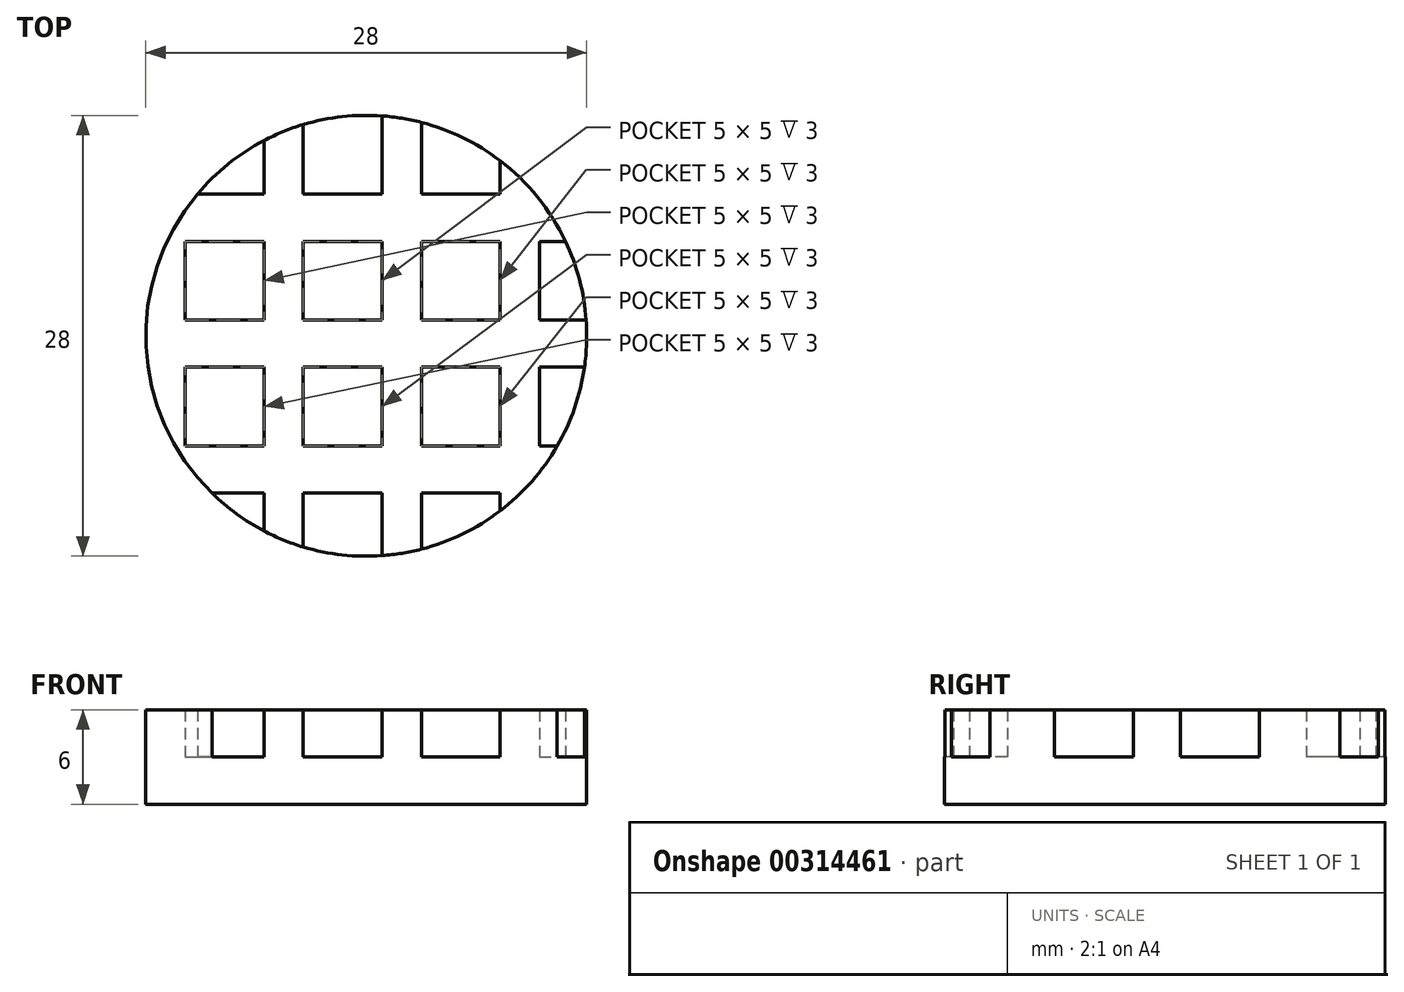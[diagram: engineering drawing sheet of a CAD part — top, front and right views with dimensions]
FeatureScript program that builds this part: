
annotation { "Feature Type Name" : "Feature", "Feature Type Description" : "" }
export const myFeature = defineFeature(function(context is Context, id is Id, definition is map)
    precondition{}
    {
        {
            var Q0;
            Q0=qCreatedBy(makeId("Top.planeOp"),FACE);
            var sketch = newSketch(context, id + "F0", { "sketchPlane" : qUnion([Q0])});
            skCircle(sketch, "E0", {"center": v(0, 0) * mm, "radius": 14 * mm});
            skSolve(sketch);
        }
        {
            var Q0;
            Q0=makeQuery(id+"F0.imprint","IMPRINT",FACE,{"disambiguationData":[TD([[makeQuery(id+"F0.imprint","IMPRINT",EDGE,{"derivedFrom":sQuery(id+"F0.wireOp",EDGE,"E0")}),1.0]])]});
            extrude(context, id + "F1", {"entities" : qUnion([Q0]), "depth" : 3 * mm});
        }
        {
            var Q0;
            Q0=makeQuery(id+"F1.opExtrude","CAP_FACE",FACE,{"disambiguationData":[OSD([sQuery(id+"F0.wireOp",EDGE,"E0")])],"isStart":false});
            var sketch = newSketch(context, id + "F2", { "sketchPlane" : qUnion([Q0])});
            skLineSegment(sketch, "E1.bottom", {"start": v(-11.5, 14) * mm, "end": v(-6.5, 14) * mm});
            skLineSegment(sketch, "E1.top", {"start": v(-11.5, 9) * mm, "end": v(-6.5, 9) * mm});
            skLineSegment(sketch, "E1.left", {"start": v(-11.5, 14) * mm, "end": v(-11.5, 9) * mm});
            skLineSegment(sketch, "E1.right", {"start": v(-6.5, 14) * mm, "end": v(-6.5, 9) * mm});
            skLineSegment(sketch, "E2.1.0.0", {"start": v(-4, 9) * mm, "end": v(1, 9) * mm});
            skLineSegment(sketch, "E2.1.0.1", {"start": v(-4, 14) * mm, "end": v(-4, 9) * mm});
            skLineSegment(sketch, "E2.1.0.2", {"start": v(1, 14) * mm, "end": v(1, 9) * mm});
            skLineSegment(sketch, "E2.1.0.3", {"start": v(-4, 14) * mm, "end": v(1, 14) * mm});
            skLineSegment(sketch, "E2.2.0.0", {"start": v(3.5, 9) * mm, "end": v(8.5, 9) * mm});
            skLineSegment(sketch, "E2.2.0.1", {"start": v(3.5, 14) * mm, "end": v(3.5, 9) * mm});
            skLineSegment(sketch, "E2.2.0.2", {"start": v(8.5, 14) * mm, "end": v(8.5, 9) * mm});
            skLineSegment(sketch, "E2.2.0.3", {"start": v(3.5, 14) * mm, "end": v(8.5, 14) * mm});
            skLineSegment(sketch, "E2.direction1", {"start": v(-11.5, 9) * mm, "end": v(-4, 9) * mm, "construction": true});
            skLineSegment(sketch, "E3.0.3.0", {"start": v(11, 9) * mm, "end": v(16, 9) * mm});
            skLineSegment(sketch, "E3.3.3.0", {"start": v(11, 14) * mm, "end": v(11, 9) * mm});
            skLineSegment(sketch, "E3.6.3.0", {"start": v(16, 14) * mm, "end": v(16, 9) * mm});
            skLineSegment(sketch, "E3.9.3.0", {"start": v(11, 14) * mm, "end": v(16, 14) * mm});
            skLineSegment(sketch, "E4.0.4.0", {"start": v(18.5, 9) * mm, "end": v(23.5, 9) * mm});
            skLineSegment(sketch, "E4.3.4.0", {"start": v(18.5, 14) * mm, "end": v(18.5, 9) * mm});
            skLineSegment(sketch, "E4.6.4.0", {"start": v(23.5, 14) * mm, "end": v(23.5, 9) * mm});
            skLineSegment(sketch, "E4.9.4.0", {"start": v(18.5, 14) * mm, "end": v(23.5, 14) * mm});
            skLineSegment(sketch, "E5.0.5.0", {"start": v(26, 9) * mm, "end": v(31, 9) * mm});
            skLineSegment(sketch, "E5.3.5.0", {"start": v(26, 14) * mm, "end": v(26, 9) * mm});
            skLineSegment(sketch, "E5.6.5.0", {"start": v(31, 14) * mm, "end": v(31, 9) * mm});
            skLineSegment(sketch, "E5.9.5.0", {"start": v(26, 14) * mm, "end": v(31, 14) * mm});
            skLineSegment(sketch, "E6.0.6.0", {"start": v(33.5, 9) * mm, "end": v(38.5, 9) * mm});
            skLineSegment(sketch, "E6.3.6.0", {"start": v(33.5, 14) * mm, "end": v(33.5, 9) * mm});
            skLineSegment(sketch, "E6.6.6.0", {"start": v(38.5, 14) * mm, "end": v(38.5, 9) * mm});
            skLineSegment(sketch, "E6.9.6.0", {"start": v(33.5, 14) * mm, "end": v(38.5, 14) * mm});
            skLineSegment(sketch, "E6.0.7.0", {"start": v(41, 9) * mm, "end": v(46, 9) * mm});
            skLineSegment(sketch, "E6.3.7.0", {"start": v(41, 14) * mm, "end": v(41, 9) * mm});
            skLineSegment(sketch, "E6.6.7.0", {"start": v(46, 14) * mm, "end": v(46, 9) * mm});
            skLineSegment(sketch, "E6.9.7.0", {"start": v(41, 14) * mm, "end": v(46, 14) * mm});
            skLineSegment(sketch, "E7.1.0.0", {"start": v(3.5, 6) * mm, "end": v(3.5, 1) * mm});
            skLineSegment(sketch, "E7.1.0.1", {"start": v(-19, 1) * mm, "end": v(-11.5, 1) * mm, "construction": true});
            skLineSegment(sketch, "E7.1.0.2", {"start": v(-6.5, 6) * mm, "end": v(-6.5, 1) * mm});
            skLineSegment(sketch, "E7.1.0.3", {"start": v(-4, 6) * mm, "end": v(-4, 1) * mm});
            skLineSegment(sketch, "E7.1.0.4", {"start": v(3.5, 1) * mm, "end": v(8.5, 1) * mm});
            skLineSegment(sketch, "E7.1.0.5", {"start": v(31, 6) * mm, "end": v(31, 1) * mm});
            skLineSegment(sketch, "E7.1.0.6", {"start": v(26, 1) * mm, "end": v(31, 1) * mm});
            skLineSegment(sketch, "E7.1.0.7", {"start": v(-11.5, 6) * mm, "end": v(-11.5, 1) * mm});
            skLineSegment(sketch, "E7.1.0.8", {"start": v(18.5, 6) * mm, "end": v(18.5, 1) * mm});
            skLineSegment(sketch, "E7.1.0.9", {"start": v(38.5, 6) * mm, "end": v(38.5, 1) * mm});
            skLineSegment(sketch, "E7.1.0.10", {"start": v(8.5, 6) * mm, "end": v(8.5, 1) * mm});
            skLineSegment(sketch, "E7.1.0.11", {"start": v(-11.5, 1) * mm, "end": v(-6.5, 1) * mm});
            skLineSegment(sketch, "E7.1.0.12", {"start": v(26, 6) * mm, "end": v(31, 6) * mm});
            skLineSegment(sketch, "E7.1.0.13", {"start": v(11, 1) * mm, "end": v(16, 1) * mm});
            skLineSegment(sketch, "E7.1.0.14", {"start": v(3.5, 6) * mm, "end": v(8.5, 6) * mm});
            skLineSegment(sketch, "E7.1.0.15", {"start": v(1, 6) * mm, "end": v(1, 1) * mm});
            skLineSegment(sketch, "E7.1.0.16", {"start": v(11, 6) * mm, "end": v(16, 6) * mm});
            skLineSegment(sketch, "E7.1.0.17", {"start": v(33.5, 6) * mm, "end": v(33.5, 1) * mm});
            skLineSegment(sketch, "E7.1.0.18", {"start": v(23.5, 6) * mm, "end": v(23.5, 1) * mm});
            skLineSegment(sketch, "E7.1.0.19", {"start": v(33.5, 1) * mm, "end": v(38.5, 1) * mm});
            skLineSegment(sketch, "E7.1.0.20", {"start": v(11, 6) * mm, "end": v(11, 1) * mm});
            skLineSegment(sketch, "E7.1.0.21", {"start": v(18.5, 6) * mm, "end": v(23.5, 6) * mm});
            skLineSegment(sketch, "E7.1.0.22", {"start": v(-14, 6) * mm, "end": v(-14, 1) * mm});
            skLineSegment(sketch, "E7.1.0.23", {"start": v(-19, 6) * mm, "end": v(-14, 6) * mm});
            skLineSegment(sketch, "E7.1.0.24", {"start": v(-4, 6) * mm, "end": v(1, 6) * mm});
            skLineSegment(sketch, "E7.1.0.25", {"start": v(-4, 1) * mm, "end": v(1, 1) * mm});
            skLineSegment(sketch, "E7.1.0.26", {"start": v(-11.5, 6) * mm, "end": v(-6.5, 6) * mm});
            skLineSegment(sketch, "E7.1.0.27", {"start": v(-19, 6) * mm, "end": v(-19, 1) * mm});
            skLineSegment(sketch, "E7.1.0.28", {"start": v(18.5, 1) * mm, "end": v(23.5, 1) * mm});
            skLineSegment(sketch, "E7.1.0.29", {"start": v(33.5, 6) * mm, "end": v(38.5, 6) * mm});
            skLineSegment(sketch, "E7.1.0.30", {"start": v(26, 6) * mm, "end": v(26, 1) * mm});
            skLineSegment(sketch, "E7.1.0.31", {"start": v(16, 6) * mm, "end": v(16, 1) * mm});
            skLineSegment(sketch, "E7.1.0.32", {"start": v(-19, 1) * mm, "end": v(-14, 1) * mm});
            skLineSegment(sketch, "E7.2.0.0", {"start": v(-4, -2) * mm, "end": v(-4, -7) * mm});
            skLineSegment(sketch, "E7.2.0.1", {"start": v(-26.5, -7) * mm, "end": v(-19, -7) * mm, "construction": true});
            skLineSegment(sketch, "E7.2.0.2", {"start": v(-14, -2) * mm, "end": v(-14, -7) * mm});
            skLineSegment(sketch, "E7.2.0.3", {"start": v(-11.5, -2) * mm, "end": v(-11.5, -7) * mm});
            skLineSegment(sketch, "E7.2.0.4", {"start": v(-4, -7) * mm, "end": v(1, -7) * mm});
            skLineSegment(sketch, "E7.2.0.5", {"start": v(23.5, -2) * mm, "end": v(23.5, -7) * mm});
            skLineSegment(sketch, "E7.2.0.6", {"start": v(18.5, -7) * mm, "end": v(23.5, -7) * mm});
            skLineSegment(sketch, "E7.2.0.7", {"start": v(-19, -2) * mm, "end": v(-19, -7) * mm});
            skLineSegment(sketch, "E7.2.0.8", {"start": v(11, -2) * mm, "end": v(11, -7) * mm});
            skLineSegment(sketch, "E7.2.0.9", {"start": v(31, -2) * mm, "end": v(31, -7) * mm});
            skLineSegment(sketch, "E7.2.0.10", {"start": v(1, -2) * mm, "end": v(1, -7) * mm});
            skLineSegment(sketch, "E7.2.0.11", {"start": v(-19, -7) * mm, "end": v(-14, -7) * mm});
            skLineSegment(sketch, "E7.2.0.12", {"start": v(18.5, -2) * mm, "end": v(23.5, -2) * mm});
            skLineSegment(sketch, "E7.2.0.13", {"start": v(3.5, -7) * mm, "end": v(8.5, -7) * mm});
            skLineSegment(sketch, "E7.2.0.14", {"start": v(-4, -2) * mm, "end": v(1, -2) * mm});
            skLineSegment(sketch, "E7.2.0.15", {"start": v(-6.5, -2) * mm, "end": v(-6.5, -7) * mm});
            skLineSegment(sketch, "E7.2.0.16", {"start": v(3.5, -2) * mm, "end": v(8.5, -2) * mm});
            skLineSegment(sketch, "E7.2.0.17", {"start": v(26, -2) * mm, "end": v(26, -7) * mm});
            skLineSegment(sketch, "E7.2.0.18", {"start": v(16, -2) * mm, "end": v(16, -7) * mm});
            skLineSegment(sketch, "E7.2.0.19", {"start": v(26, -7) * mm, "end": v(31, -7) * mm});
            skLineSegment(sketch, "E7.2.0.20", {"start": v(3.5, -2) * mm, "end": v(3.5, -7) * mm});
            skLineSegment(sketch, "E7.2.0.21", {"start": v(11, -2) * mm, "end": v(16, -2) * mm});
            skLineSegment(sketch, "E7.2.0.22", {"start": v(-21.5, -2) * mm, "end": v(-21.5, -7) * mm});
            skLineSegment(sketch, "E7.2.0.23", {"start": v(-26.5, -2) * mm, "end": v(-21.5, -2) * mm});
            skLineSegment(sketch, "E7.2.0.24", {"start": v(-11.5, -2) * mm, "end": v(-6.5, -2) * mm});
            skLineSegment(sketch, "E7.2.0.25", {"start": v(-11.5, -7) * mm, "end": v(-6.5, -7) * mm});
            skLineSegment(sketch, "E7.2.0.26", {"start": v(-19, -2) * mm, "end": v(-14, -2) * mm});
            skLineSegment(sketch, "E7.2.0.27", {"start": v(-26.5, -2) * mm, "end": v(-26.5, -7) * mm});
            skLineSegment(sketch, "E7.2.0.28", {"start": v(11, -7) * mm, "end": v(16, -7) * mm});
            skLineSegment(sketch, "E7.2.0.29", {"start": v(26, -2) * mm, "end": v(31, -2) * mm});
            skLineSegment(sketch, "E7.2.0.30", {"start": v(18.5, -2) * mm, "end": v(18.5, -7) * mm});
            skLineSegment(sketch, "E7.2.0.31", {"start": v(8.5, -2) * mm, "end": v(8.5, -7) * mm});
            skLineSegment(sketch, "E7.2.0.32", {"start": v(-26.5, -7) * mm, "end": v(-21.5, -7) * mm});
            skLineSegment(sketch, "E7.direction1", {"start": v(-11.5, 9) * mm, "end": v(-19, 1) * mm, "construction": true});
            skLineSegment(sketch, "E8.0.3.0", {"start": v(-11.5, -10) * mm, "end": v(-11.5, -15) * mm});
            skLineSegment(sketch, "E8.3.3.0", {"start": v(-34, -15) * mm, "end": v(-26.5, -15) * mm, "construction": true});
            skLineSegment(sketch, "E8.6.3.0", {"start": v(-21.5, -10) * mm, "end": v(-21.5, -15) * mm});
            skLineSegment(sketch, "E8.9.3.0", {"start": v(-19, -10) * mm, "end": v(-19, -15) * mm});
            skLineSegment(sketch, "E8.12.3.0", {"start": v(-11.5, -15) * mm, "end": v(-6.5, -15) * mm});
            skLineSegment(sketch, "E8.15.3.0", {"start": v(16, -10) * mm, "end": v(16, -15) * mm});
            skLineSegment(sketch, "E8.18.3.0", {"start": v(11, -15) * mm, "end": v(16, -15) * mm});
            skLineSegment(sketch, "E8.21.3.0", {"start": v(-26.5, -10) * mm, "end": v(-26.5, -15) * mm});
            skLineSegment(sketch, "E8.24.3.0", {"start": v(3.5, -10) * mm, "end": v(3.5, -15) * mm});
            skLineSegment(sketch, "E8.27.3.0", {"start": v(23.5, -10) * mm, "end": v(23.5, -15) * mm});
            skLineSegment(sketch, "E8.30.3.0", {"start": v(-6.5, -10) * mm, "end": v(-6.5, -15) * mm});
            skLineSegment(sketch, "E8.33.3.0", {"start": v(-26.5, -15) * mm, "end": v(-21.5, -15) * mm});
            skLineSegment(sketch, "E8.36.3.0", {"start": v(11, -10) * mm, "end": v(16, -10) * mm});
            skLineSegment(sketch, "E8.39.3.0", {"start": v(-4, -15) * mm, "end": v(1, -15) * mm});
            skLineSegment(sketch, "E8.42.3.0", {"start": v(-11.5, -10) * mm, "end": v(-6.5, -10) * mm});
            skLineSegment(sketch, "E8.45.3.0", {"start": v(-14, -10) * mm, "end": v(-14, -15) * mm});
            skLineSegment(sketch, "E8.48.3.0", {"start": v(-4, -10) * mm, "end": v(1, -10) * mm});
            skLineSegment(sketch, "E8.51.3.0", {"start": v(18.5, -10) * mm, "end": v(18.5, -15) * mm});
            skLineSegment(sketch, "E8.54.3.0", {"start": v(8.5, -10) * mm, "end": v(8.5, -15) * mm});
            skLineSegment(sketch, "E8.57.3.0", {"start": v(18.5, -15) * mm, "end": v(23.5, -15) * mm});
            skLineSegment(sketch, "E8.60.3.0", {"start": v(-4, -10) * mm, "end": v(-4, -15) * mm});
            skLineSegment(sketch, "E8.63.3.0", {"start": v(3.5, -10) * mm, "end": v(8.5, -10) * mm});
            skLineSegment(sketch, "E8.66.3.0", {"start": v(-29, -10) * mm, "end": v(-29, -15) * mm});
            skLineSegment(sketch, "E8.69.3.0", {"start": v(-34, -10) * mm, "end": v(-29, -10) * mm});
            skLineSegment(sketch, "E8.72.3.0", {"start": v(-19, -10) * mm, "end": v(-14, -10) * mm});
            skLineSegment(sketch, "E8.75.3.0", {"start": v(-19, -15) * mm, "end": v(-14, -15) * mm});
            skLineSegment(sketch, "E8.78.3.0", {"start": v(-26.5, -10) * mm, "end": v(-21.5, -10) * mm});
            skLineSegment(sketch, "E8.81.3.0", {"start": v(-34, -10) * mm, "end": v(-34, -15) * mm});
            skLineSegment(sketch, "E8.84.3.0", {"start": v(3.5, -15) * mm, "end": v(8.5, -15) * mm});
            skLineSegment(sketch, "E8.87.3.0", {"start": v(18.5, -10) * mm, "end": v(23.5, -10) * mm});
            skLineSegment(sketch, "E8.90.3.0", {"start": v(11, -10) * mm, "end": v(11, -15) * mm});
            skLineSegment(sketch, "E8.93.3.0", {"start": v(1, -10) * mm, "end": v(1, -15) * mm});
            skLineSegment(sketch, "E8.96.3.0", {"start": v(-34, -15) * mm, "end": v(-29, -15) * mm});
            skLineSegment(sketch, "E8.0.4.0", {"start": v(-19, -18) * mm, "end": v(-19, -23) * mm});
            skLineSegment(sketch, "E8.3.4.0", {"start": v(-41.5, -23) * mm, "end": v(-34, -23) * mm, "construction": true});
            skLineSegment(sketch, "E8.6.4.0", {"start": v(-29, -18) * mm, "end": v(-29, -23) * mm});
            skLineSegment(sketch, "E8.9.4.0", {"start": v(-26.5, -18) * mm, "end": v(-26.5, -23) * mm});
            skLineSegment(sketch, "E8.12.4.0", {"start": v(-19, -23) * mm, "end": v(-14, -23) * mm});
            skLineSegment(sketch, "E8.15.4.0", {"start": v(8.5, -18) * mm, "end": v(8.5, -23) * mm});
            skLineSegment(sketch, "E8.18.4.0", {"start": v(3.5, -23) * mm, "end": v(8.5, -23) * mm});
            skLineSegment(sketch, "E8.21.4.0", {"start": v(-34, -18) * mm, "end": v(-34, -23) * mm});
            skLineSegment(sketch, "E8.24.4.0", {"start": v(-4, -18) * mm, "end": v(-4, -23) * mm});
            skLineSegment(sketch, "E8.27.4.0", {"start": v(16, -18) * mm, "end": v(16, -23) * mm});
            skLineSegment(sketch, "E8.30.4.0", {"start": v(-14, -18) * mm, "end": v(-14, -23) * mm});
            skLineSegment(sketch, "E8.33.4.0", {"start": v(-34, -23) * mm, "end": v(-29, -23) * mm});
            skLineSegment(sketch, "E8.36.4.0", {"start": v(3.5, -18) * mm, "end": v(8.5, -18) * mm});
            skLineSegment(sketch, "E8.39.4.0", {"start": v(-11.5, -23) * mm, "end": v(-6.5, -23) * mm});
            skLineSegment(sketch, "E8.42.4.0", {"start": v(-19, -18) * mm, "end": v(-14, -18) * mm});
            skLineSegment(sketch, "E8.45.4.0", {"start": v(-21.5, -18) * mm, "end": v(-21.5, -23) * mm});
            skLineSegment(sketch, "E8.48.4.0", {"start": v(-11.5, -18) * mm, "end": v(-6.5, -18) * mm});
            skLineSegment(sketch, "E8.51.4.0", {"start": v(11, -18) * mm, "end": v(11, -23) * mm});
            skLineSegment(sketch, "E8.54.4.0", {"start": v(1, -18) * mm, "end": v(1, -23) * mm});
            skLineSegment(sketch, "E8.57.4.0", {"start": v(11, -23) * mm, "end": v(16, -23) * mm});
            skLineSegment(sketch, "E8.60.4.0", {"start": v(-11.5, -18) * mm, "end": v(-11.5, -23) * mm});
            skLineSegment(sketch, "E8.63.4.0", {"start": v(-4, -18) * mm, "end": v(1, -18) * mm});
            skLineSegment(sketch, "E8.66.4.0", {"start": v(-36.5, -18) * mm, "end": v(-36.5, -23) * mm});
            skLineSegment(sketch, "E8.69.4.0", {"start": v(-41.5, -18) * mm, "end": v(-36.5, -18) * mm});
            skLineSegment(sketch, "E8.72.4.0", {"start": v(-26.5, -18) * mm, "end": v(-21.5, -18) * mm});
            skLineSegment(sketch, "E8.75.4.0", {"start": v(-26.5, -23) * mm, "end": v(-21.5, -23) * mm});
            skLineSegment(sketch, "E8.78.4.0", {"start": v(-34, -18) * mm, "end": v(-29, -18) * mm});
            skLineSegment(sketch, "E8.81.4.0", {"start": v(-41.5, -18) * mm, "end": v(-41.5, -23) * mm});
            skLineSegment(sketch, "E8.84.4.0", {"start": v(-4, -23) * mm, "end": v(1, -23) * mm});
            skLineSegment(sketch, "E8.87.4.0", {"start": v(11, -18) * mm, "end": v(16, -18) * mm});
            skLineSegment(sketch, "E8.90.4.0", {"start": v(3.5, -18) * mm, "end": v(3.5, -23) * mm});
            skLineSegment(sketch, "E8.93.4.0", {"start": v(-6.5, -18) * mm, "end": v(-6.5, -23) * mm});
            skLineSegment(sketch, "E8.96.4.0", {"start": v(-41.5, -23) * mm, "end": v(-36.5, -23) * mm});
            skSolve(sketch);
        }
        {
            var Q0;
            {var subQ1=sQuery(id+"F2.wireOp",EDGE,"E2.1.0.0");Q0=makeQuery(id+"F2.imprint","IMPRINT",FACE,{"disambiguationData":[TD([[makeQuery(id+"F2.imprint","IMPRINT",EDGE,{"derivedFrom":subQ1}),-1.0]])]});}
            extrude(context, id + "F3", {"entities" : qUnion([Q0]), "operationType" : NewBodyOperationType.ADD, "depth" : 3 * mm});
        }
    });
